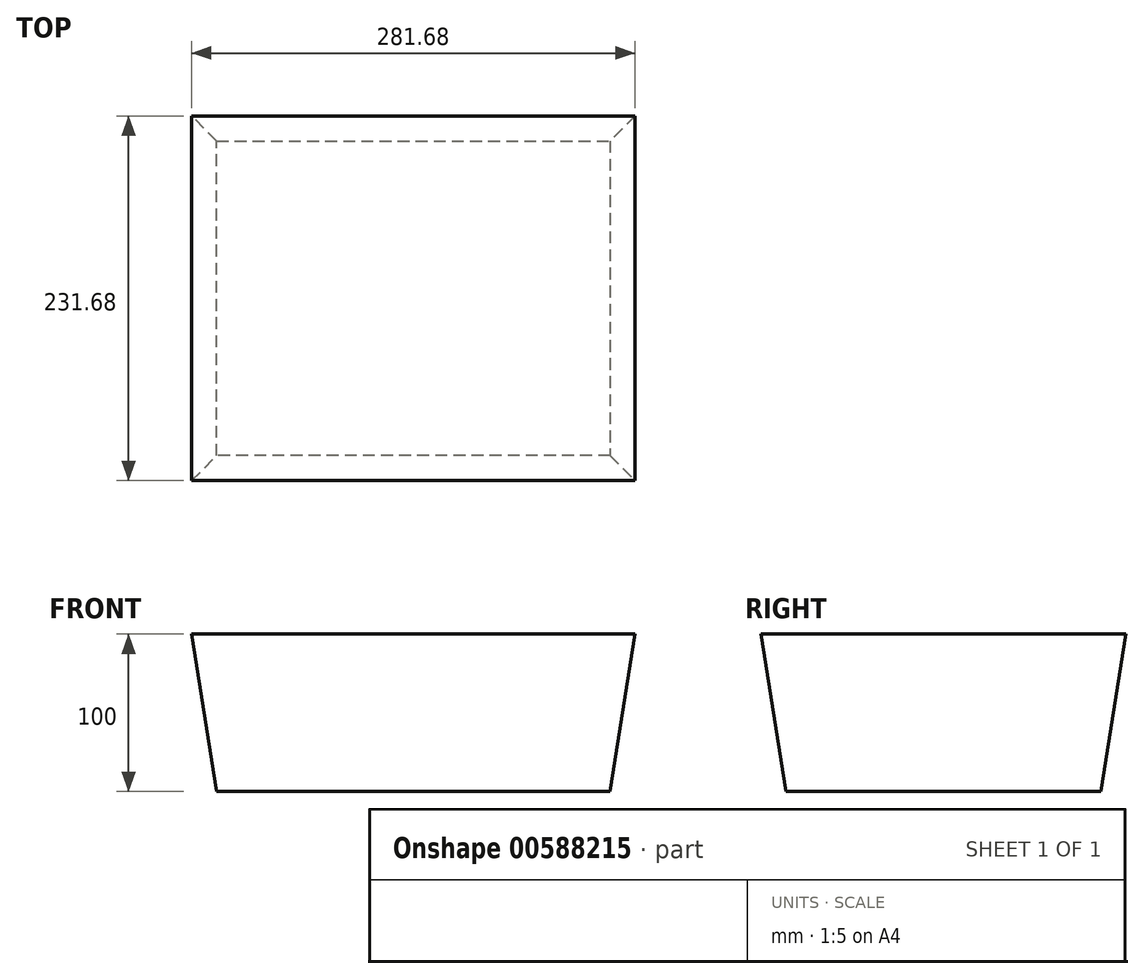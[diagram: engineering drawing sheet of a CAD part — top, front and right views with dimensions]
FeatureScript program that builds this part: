
annotation { "Feature Type Name" : "Feature", "Feature Type Description" : "" }
export const myFeature = defineFeature(function(context is Context, id is Id, definition is map)
    precondition{}
    {
        {
            var Q0;
            Q0=qCreatedBy(makeId("Top.planeOp"),FACE);
            var sketch = newSketch(context, id + "F0", { "sketchPlane" : qUnion([Q0])});
            skLineSegment(sketch, "E0.bottom", {"start": v(-125, 100) * mm, "end": v(125, 100) * mm});
            skLineSegment(sketch, "E0.top", {"start": v(-125, -100) * mm, "end": v(125, -100) * mm});
            skLineSegment(sketch, "E0.left", {"start": v(-125, 100) * mm, "end": v(-125, -100) * mm});
            skLineSegment(sketch, "E0.right", {"start": v(125, 100) * mm, "end": v(125, -100) * mm});
            skSolve(sketch);
        }
        {
            var Q0;
            Q0=makeQuery(id+"F0.imprint","IMPRINT",FACE,{"disambiguationData":[TD([[makeQuery(id+"F0.imprint","IMPRINT",EDGE,{"derivedFrom":sQuery(id+"F0.wireOp",EDGE,"E0.bottom")}),-1.0]])]});
            extrude(context, id + "F1", {"entities" : qUnion([Q0]), "depth" : 100 * mm, "offsetDistance" : 25 * mm, "hasDraft" : true, "draftAngle" : 9 * degree});
        }
        {
            var Q0;
            Q0=makeQuery(id+"F1.opExtrude","CAP_FACE",FACE,{"disambiguationData":[OSD([sQuery(id+"F0.wireOp",EDGE,"E0.bottom"),sQuery(id+"F0.wireOp",EDGE,"E0.top"),sQuery(id+"F0.wireOp",EDGE,"E0.left"),sQuery(id+"F0.wireOp",EDGE,"E0.right")])],"isStart":false});
            var sketch = newSketch(context, id + "F2", { "sketchPlane" : qUnion([Q0])});
            skLineSegment(sketch, "E1.bottom", {"start": v(-133.34, 108.34) * mm, "end": v(-118.34, 108.34) * mm});
            skLineSegment(sketch, "E1.top", {"start": v(-133.34, 93.34) * mm, "end": v(-118.34, 93.34) * mm});
            skLineSegment(sketch, "E1.left", {"start": v(-133.34, 108.34) * mm, "end": v(-133.34, 93.34) * mm});
            skLineSegment(sketch, "E1.right", {"start": v(-118.34, 108.34) * mm, "end": v(-118.34, 93.34) * mm});
            skPoint(sketch, "E1.middle", {"position": v(-125.84, 100.84) * mm});
            skSolve(sketch);
        }
        {
            var Q0;
            Q0=sQuery(id+"F2.wireOp",EDGE,"E1.top");
            var Q1;
            Q1=sQuery(id+"F2.wireOp",EDGE,"E1.left");
            var Q2;
            Q2=sQuery(id+"F2.wireOp",EDGE,"E1.right");
            var Q3;
            Q3=sQuery(id+"F2.wireOp",EDGE,"E1.bottom");
            extrude(context, id + "F3", {"bodyType" : ToolBodyType.SURFACE, "surfaceEntities" : qUnion([Q0, Q1, Q2, Q3]), "depth" : 150 * mm, "offsetDistance" : 25 * mm});
        }
    });
